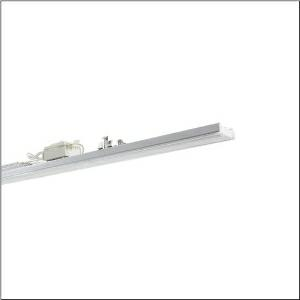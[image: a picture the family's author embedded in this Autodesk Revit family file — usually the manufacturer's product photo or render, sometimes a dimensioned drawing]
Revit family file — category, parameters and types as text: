
# Revit family: licross_r__21_recessed_ho_52tl18cn4c5m_5c60
name_source: partatom
category: Lighting Fixtures
units: mm (PartAtom-declared; Revit-internal decimal feet)

## family parameters
Cut with Voids When Loaded = No
Host = Face
Light Source = No
Part Type = Normal
Room Calculation Point = No
Round Connector Dimension = Use Diameter
Shared = No

## types (1)
- --- (1 x LED, 12540 lm, 68.4 W, 4000K)
    Apparent Load = 68 VA
    CIE Flux Codes = 75 94 99 100 100
    Color Rendering = 80
    Color Temperature = 4000K
    Default Elevation = 1800 mm
    Description = Licross® 21 Recessed HO, luminaire insert, of sheet steel, galvanised, coil coated, white, length: 1.500mm, width: 66mm, height: 67mm, LED rated luminous flux: 12.540lm, light colour: 840, control gear: ON/OFF Multilumen, CLOi, control gear: ECG Multilumen, with plug, 3-pole, with phase selection, mains connection: 220..240V, AC, 50/60Hz, internal wiring halogen-free, primary light control with lens, of plastic, primary optical cover: cover, of PMMA, light emission: direct distribution, primary light characteristic: symmetric, protection rating (complete): IP40, insulation class (complete): insulation class I (protective earthing), certification: CE, ENEC, VDE, UKCA, protection symbol: D if used in an environment without relevant dust loads with corresponding accessories, impact resistance: IK06, permissible ambient temperature for indoor applications: -35..+30°C, corresponds to IFS (International Featured Standards) requirements for safety and quality in the food industry, reducing of maximum allowable ambient temperature of 5°C with ceiling mounting, LABS conformity tested according to VDMA 24364:2018-05, packaging unit: 1 piece
    Height = 58 mm
    Lamp = 1 x LED
    Lamp Light Flux = 12540 lm
    Lamp Power = 68.4 W
    Lamp count = 1
    Length = 1500 mm
    Luminous efficacy = 183 lm/W
    Manufacturer = Siteco
    ModVariant = No
    Model = 52TL18CN4C5M
    Mounting Place = Ceiling
    Mounting Type = Pendant
    Number of Poles = 1
    OnlyDefault = Yes
    Power Factor = 1
    Product Name = Licross® 21 Recessed HO
    Product group = luminaire insert | ceiling pendant
    ProductGroupID = 902
    Protection Class = Protection class I
    Protection Degree = IP 40
    RLX_Detail_Level = 1
    RLX_Emergency_Light_Flux = 0 lm
    RLX_Emergency_Type = 0
    RLX_Emergency_Type_DB = No
    RlxData = <blob elided: 22337 chars, md5=32e1b8e5>
    Socket = socket
    Standby Power = 0 W
    System Light Flux = 12540 lm
    System Power = 68 W
    Type Comments = factory setting: luminous flux: 100 % | (A | C | E) | 161 mA
    Type Image = l_1296930.jpg
    URL = http://relux.com
    VarID = @adj_131435
    Voltage = 0 V
    Weight = 0.00 kg
    Width = 66 mm

## geometry (parser evidence)
native form markers: Blend x4, Sweep x10
no freeform markers — native parametric forms only
